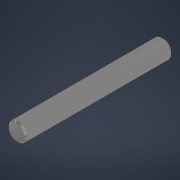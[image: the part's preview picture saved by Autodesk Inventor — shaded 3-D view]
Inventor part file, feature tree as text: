
AUTODESK INVENTOR PART (.ipt)
format: ipt  version: 2022.1 (Build 261234000, 234)  size: 90,112 bytes
history: native  units: mm
features: extrude x1, chamfer x1, sketch x1
ambient origin geometry x8: Origin, YZ Plane, XZ Plane, XY Plane, X Axis, Y Axis, Z Axis, Center Point
bodies: Volumenkörper1 (feature_tree)
feature tree (3):
  extrude  "Extrusion1"  Depth=40.0mm TaperAngle=0.0deg
  chamfer  "Fase1"  Distance=0.4mm Angle=45.0deg
  sketch  "Skizze1"  dims[d0=5.0mm d1=40.0mm d2=0.0mm d3=0.4mm d4=2.0mm d5=45.0deg]
